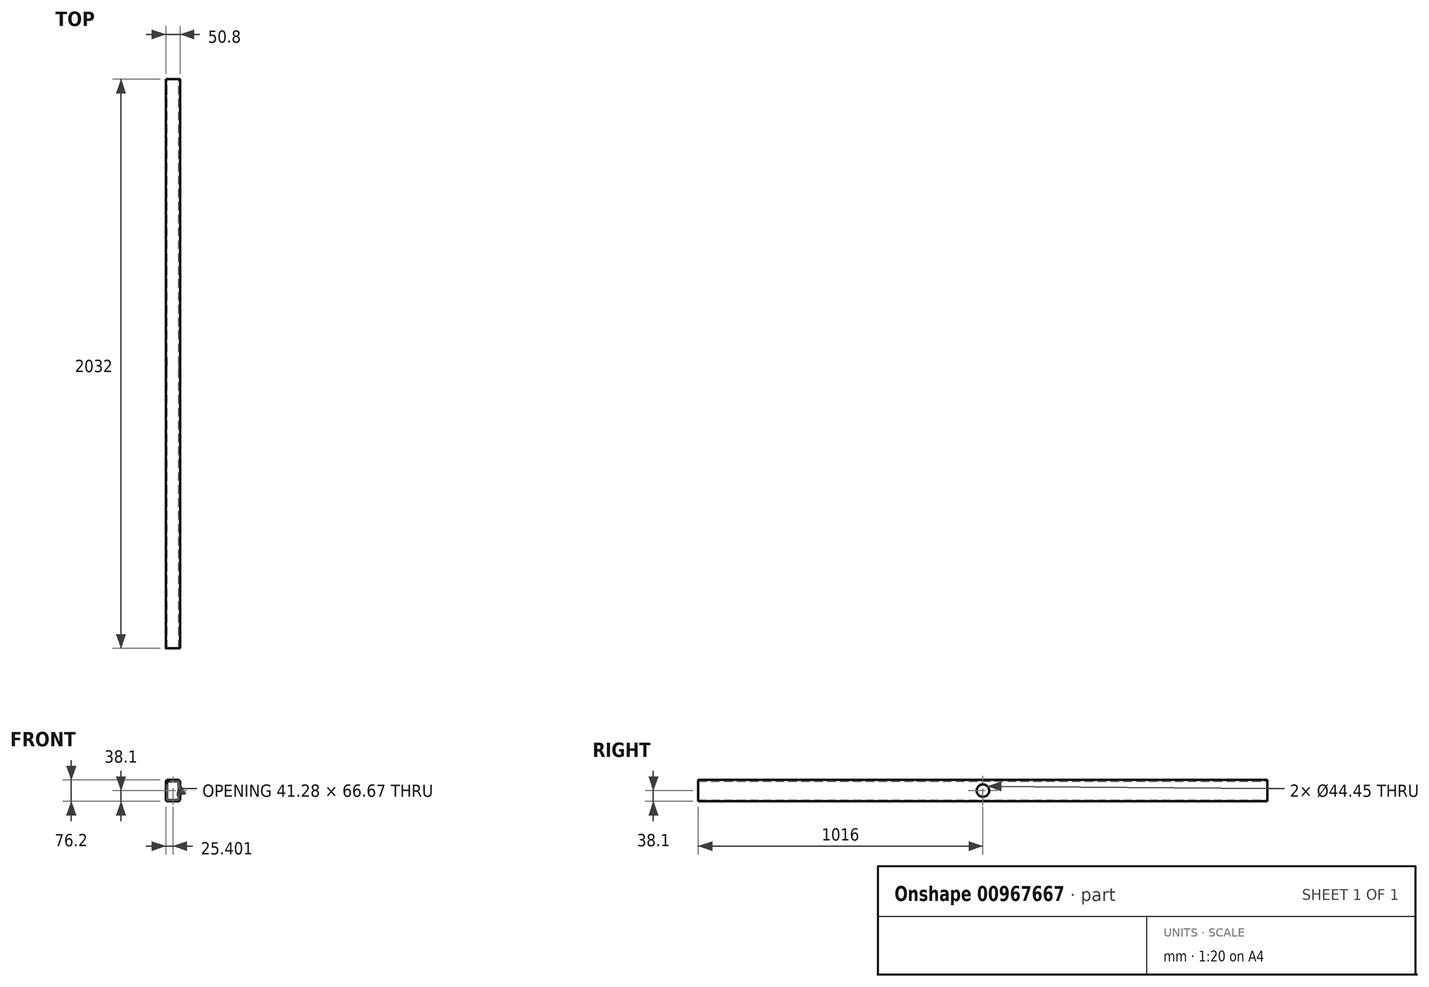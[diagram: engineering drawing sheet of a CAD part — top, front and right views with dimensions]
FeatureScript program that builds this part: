
annotation { "Feature Type Name" : "Feature", "Feature Type Description" : "" }
export const myFeature = defineFeature(function(context is Context, id is Id, definition is map)
    precondition{}
    {
        {
            var Q0;
            Q0=qCreatedBy(makeId("Front.planeOp"),FACE);
            var sketch = newSketch(context, id + "F0", { "sketchPlane" : qUnion([Q0])});
            skLineSegment(sketch, "E0.bottom", {"start": v(-77.89, 16.64) * mm, "end": v(-39.79, 16.64) * mm});
            skLineSegment(sketch, "E0.top", {"start": v(-77.89, 92.84) * mm, "end": v(-39.79, 92.84) * mm});
            skLineSegment(sketch, "E0.left", {"start": v(-84.24, 23) * mm, "end": v(-84.24, 86.5) * mm});
            skLineSegment(sketch, "E0.right", {"start": v(-33.44, 23) * mm, "end": v(-33.44, 86.5) * mm});
            skPoint(sketch, "E1.visualSharp", {"position": v(-84.24, 92.84) * mm});
            skArc(sketch, "E1.filletArc", {"start": v(-77.89, 92.84) * mm, "mid": v(-82.38, 90.98) * mm, "end": v(-84.24, 86.5) * mm});
            skPoint(sketch, "E2.visualSharp", {"position": v(-33.44, 92.84) * mm});
            skArc(sketch, "E2.filletArc", {"start": v(-33.44, 86.5) * mm, "mid": v(-35.3, 90.98) * mm, "end": v(-39.79, 92.84) * mm});
            skPoint(sketch, "E3.visualSharp", {"position": v(-33.44, 16.64) * mm});
            skArc(sketch, "E3.filletArc", {"start": v(-39.79, 16.64) * mm, "mid": v(-35.3, 18.5) * mm, "end": v(-33.44, 23) * mm});
            skPoint(sketch, "E4.visualSharp", {"position": v(-84.24, 16.64) * mm});
            skArc(sketch, "E4.filletArc", {"start": v(-84.24, 23) * mm, "mid": v(-82.38, 18.5) * mm, "end": v(-77.89, 16.64) * mm});
            skArc(sketch, "E5.0", {"start": v(-77.89, 88.08) * mm, "mid": v(-79.01, 87.61) * mm, "end": v(-79.48, 86.5) * mm});
            skLineSegment(sketch, "E5.1", {"start": v(-79.48, 23) * mm, "end": v(-79.48, 86.5) * mm});
            skLineSegment(sketch, "E5.2", {"start": v(-77.89, 88.08) * mm, "end": v(-39.79, 88.08) * mm});
            skArc(sketch, "E5.3", {"start": v(-79.48, 23) * mm, "mid": v(-79.01, 21.87) * mm, "end": v(-77.89, 21.4) * mm});
            skArc(sketch, "E5.4", {"start": v(-38.2, 86.5) * mm, "mid": v(-38.67, 87.61) * mm, "end": v(-39.79, 88.08) * mm});
            skLineSegment(sketch, "E5.5", {"start": v(-38.2, 23) * mm, "end": v(-38.2, 86.5) * mm});
            skArc(sketch, "E5.6", {"start": v(-39.79, 21.4) * mm, "mid": v(-38.67, 21.87) * mm, "end": v(-38.2, 23) * mm});
            skLineSegment(sketch, "E5.7", {"start": v(-77.89, 21.4) * mm, "end": v(-39.79, 21.4) * mm});
            skSolve(sketch);
        }
        {
            var Q0;
            Q0 = qSketchRegion(id + "F0", true);
            extrude(context, id + "F1", {"entities" : qUnion([Q0]), "depth" : 2032 * mm, "offsetDistance" : 25.4 * mm});
        }
        {
            var Q0;
            Q0=makeQuery(id+"F1.opExtrude","SWEPT_FACE",FACE,{"disambiguationData":[OSD([sQuery(id+"F0.wireOp",EDGE,"E0.right")])]});
            var sketch = newSketch(context, id + "F2", { "sketchPlane" : qUnion([Q0])});
            skCircle(sketch, "E6", {"center": v(-1016, 54.74) * mm, "radius": 22.23 * mm});
            skPoint(sketch, "E6.centerSnap0", {"position": v(-1016, 86.5) * mm});
            skSolve(sketch);
        }
        {
            var Q0;
            Q0 = qSketchRegion(id + "F2", true);
            extrude(context, id + "F3", {"entities" : qUnion([Q0]), "operationType" : NewBodyOperationType.REMOVE, "endBound" : BoundingType.THROUGH_ALL, "oppositeDirection" : true, "depth" : 25.4 * mm, "offsetDistance" : 25.4 * mm});
        }
    });
